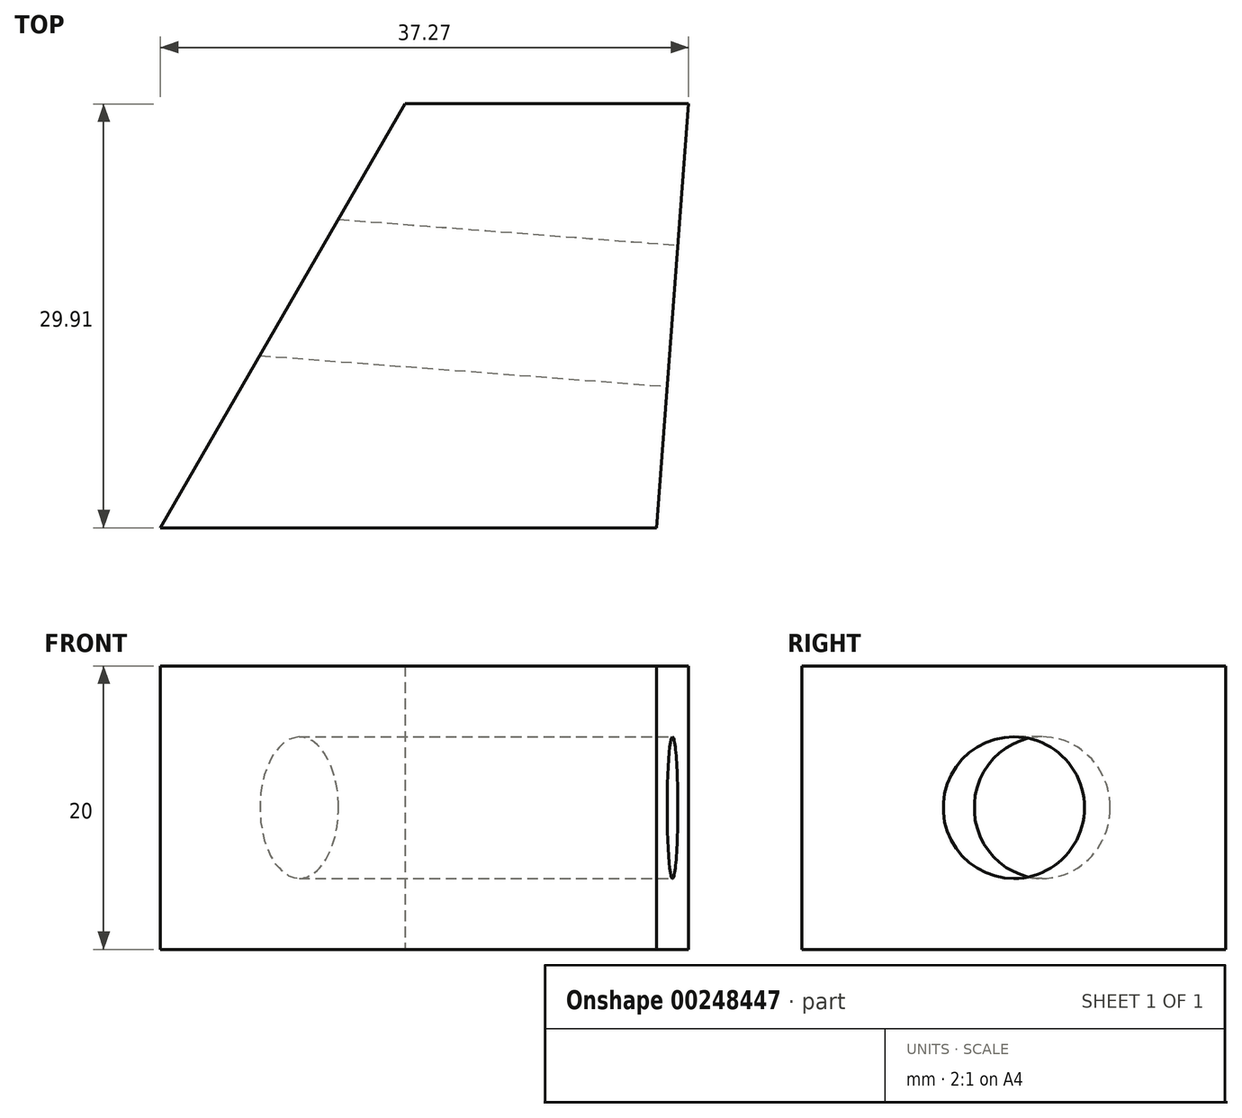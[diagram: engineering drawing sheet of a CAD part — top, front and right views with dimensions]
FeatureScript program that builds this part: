
annotation { "Feature Type Name" : "Feature", "Feature Type Description" : "" }
export const myFeature = defineFeature(function(context is Context, id is Id, definition is map)
    precondition{}
    {
        {
            var Q0;
            Q0=qCreatedBy(makeId("Top.planeOp"),FACE);
            var sketch = newSketch(context, id + "F0", { "sketchPlane" : qUnion([Q0])});
            skLineSegment(sketch, "E0", {"start": v(0, 0) * mm, "end": v(35, 0) * mm});
            skLineSegment(sketch, "E1", {"start": v(35, 0) * mm, "end": v(37.27, 29.91) * mm});
            skLineSegment(sketch, "E2", {"start": v(37.27, 29.91) * mm, "end": v(17.27, 29.91) * mm});
            skLineSegment(sketch, "E3", {"start": v(17.27, 29.91) * mm, "end": v(0, 0) * mm});
            skSolve(sketch);
        }
        {
            var Q0;
            Q0=makeQuery(id+"F0.imprint","IMPRINT",FACE,{"disambiguationData":[TD([[makeQuery(id+"F0.imprint","IMPRINT",EDGE,{"derivedFrom":sQuery(id+"F0.wireOp",EDGE,"E0")}),1.0]])]});
            extrude(context, id + "F1", {"entities" : qUnion([Q0]), "depth" : 20 * mm});
        }
        {
            var Q0;
            Q0=makeQuery(id+"F1.opExtrude","SWEPT_FACE",FACE,{"disambiguationData":[OSD([sQuery(id+"F0.wireOp",EDGE,"E1")])]});
            var sketch = newSketch(context, id + "F2", { "sketchPlane" : qUnion([Q0])});
            skCircle(sketch, "E4", {"center": v(17.65, 10) * mm, "radius": 5 * mm});
            skPoint(sketch, "E4.centerSnap0", {"position": v(17.65, 0) * mm});
            skPoint(sketch, "E4.centerSnap1", {"position": v(2.65, 10) * mm});
            skSolve(sketch);
        }
        {
            var Q0;
            Q0=makeQuery(id+"F2.imprint","IMPRINT",FACE,{"disambiguationData":[TD([[makeQuery(id+"F2.imprint","IMPRINT",EDGE,{"derivedFrom":sQuery(id+"F2.wireOp",EDGE,"E4")}),1.0]])]});
            extrude(context, id + "F3", {"entities" : qUnion([Q0]), "operationType" : NewBodyOperationType.REMOVE, "endBound" : BoundingType.THROUGH_ALL, "oppositeDirection" : true, "depth" : 25 * mm});
        }
    });
